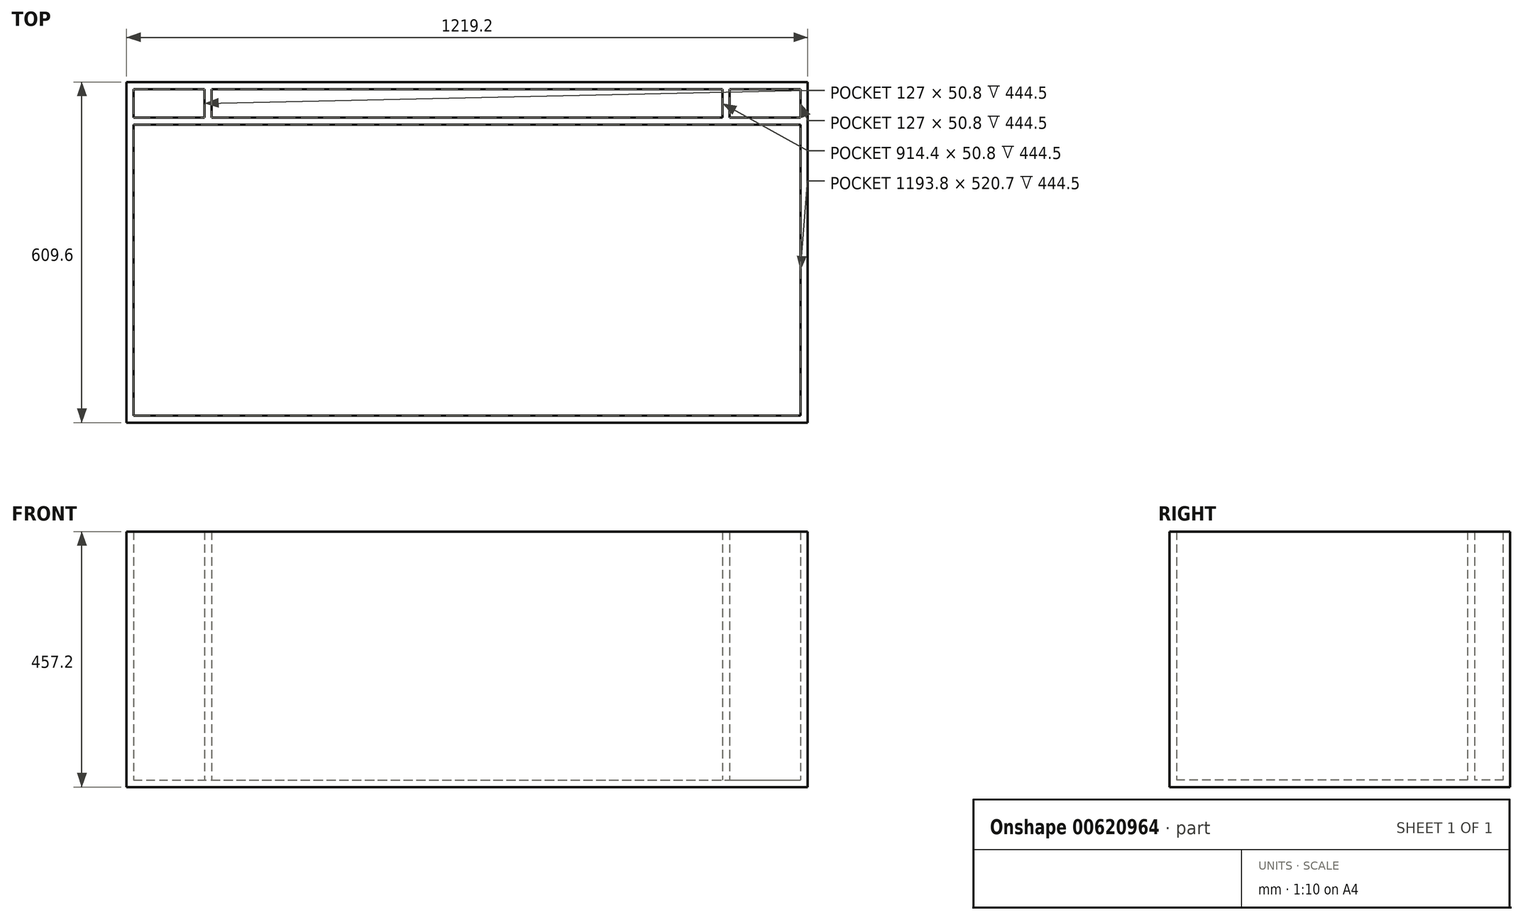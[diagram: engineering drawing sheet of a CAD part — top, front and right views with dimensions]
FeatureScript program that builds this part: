
annotation { "Feature Type Name" : "Feature", "Feature Type Description" : "" }
export const myFeature = defineFeature(function(context is Context, id is Id, definition is map)
    precondition{}
    {
        {
            var Q0;
            Q0=qCreatedBy(makeId("Top.planeOp"),FACE);
            var sketch = newSketch(context, id + "F0", { "sketchPlane" : qUnion([Q0])});
            skLineSegment(sketch, "E0.bottom", {"start": v(-605.39, 273.8) * mm, "end": v(613.81, 273.8) * mm});
            skLineSegment(sketch, "E0.top", {"start": v(-605.39, -335.8) * mm, "end": v(613.81, -335.8) * mm});
            skLineSegment(sketch, "E0.left", {"start": v(-605.39, 273.8) * mm, "end": v(-605.39, -335.8) * mm});
            skLineSegment(sketch, "E0.right", {"start": v(613.81, 273.8) * mm, "end": v(613.81, -335.8) * mm});
            skSolve(sketch);
        }
        {
            var Q0;
            Q0=makeQuery(id+"F0.imprint","IMPRINT",FACE,{"disambiguationData":[TD([[makeQuery(id+"F0.imprint","IMPRINT",EDGE,{"derivedFrom":sQuery(id+"F0.wireOp",EDGE,"E0.bottom")}),-1.0]])]});
            extrude(context, id + "F1", {"entities" : qUnion([Q0]), "depth" : 457.2 * mm, "offsetDistance" : 25.4 * mm});
        }
        {
            var Q0;
            Q0=makeQuery(id+"F1.opExtrude","CAP_FACE",FACE,{"disambiguationData":[OSD([sQuery(id+"F0.wireOp",EDGE,"E0.bottom"),sQuery(id+"F0.wireOp",EDGE,"E0.top"),sQuery(id+"F0.wireOp",EDGE,"E0.left"),sQuery(id+"F0.wireOp",EDGE,"E0.right")])],"isStart":false});
            shell(context, id + "F2", {"entities" : qUnion([Q0]), "thickness" : 12.7 * mm});
        }
        {
            var Q0;
            Q0=makeQuery(id+"F2.opShell","OFFSET_FACE",FACE,{"disambiguationData":[OSD([sQuery(id+"F0.wireOp",EDGE,"E0.bottom"),sQuery(id+"F0.wireOp",EDGE,"E0.top"),sQuery(id+"F0.wireOp",EDGE,"E0.left"),sQuery(id+"F0.wireOp",EDGE,"E0.right")])]});
            var sketch = newSketch(context, id + "F3", { "sketchPlane" : qUnion([Q0])});
            skLineSegment(sketch, "E1", {"start": v(-592.69, 210.3) * mm, "end": v(-465.69, 210.3) * mm});
            skLineSegment(sketch, "E2", {"start": v(-465.69, 261.1) * mm, "end": v(-465.69, 210.3) * mm});
            skLineSegment(sketch, "E3", {"start": v(474.11, 261.1) * mm, "end": v(474.11, 210.3) * mm});
            skLineSegment(sketch, "E4", {"start": v(-592.69, 197.6) * mm, "end": v(601.11, 197.6) * mm});
            skLineSegment(sketch, "E5", {"start": v(-452.99, 210.3) * mm, "end": v(-452.99, 261.1) * mm});
            skLineSegment(sketch, "E6", {"start": v(461.41, 210.3) * mm, "end": v(461.41, 261.1) * mm});
            skLineSegment(sketch, "E7.trimOffspring", {"start": v(-452.99, 210.3) * mm, "end": v(461.41, 210.3) * mm});
            skLineSegment(sketch, "E8.trimOffspring", {"start": v(474.11, 210.3) * mm, "end": v(601.11, 210.3) * mm});
            skSolve(sketch);
        }
        {
            var Q0;
            {var subQ6=sQuery(id+"F3.wireOp",EDGE,"E1");Q0=makeQuery(id+"F3.imprint","IMPRINT",FACE,{"disambiguationData":[TD([[makeQuery(id+"F3.imprint","IMPRINT",EDGE,{"derivedFrom":subQ6}),-1.0]])]});}
            var Q1;
            Q1=makeQuery(id+"F1.opExtrude","CAP_FACE",FACE,{"disambiguationData":[OSD([sQuery(id+"F0.wireOp",EDGE,"E0.bottom"),sQuery(id+"F0.wireOp",EDGE,"E0.top"),sQuery(id+"F0.wireOp",EDGE,"E0.left"),sQuery(id+"F0.wireOp",EDGE,"E0.right")])],"isStart":false});
            extrude(context, id + "F4", {"entities" : qUnion([Q0]), "operationType" : NewBodyOperationType.ADD, "endBound" : BoundingType.UP_TO_SURFACE, "depth" : 25.4 * mm, "endBoundEntityFace" : qUnion([Q1]), "offsetDistance" : 25.4 * mm});
        }
    });
